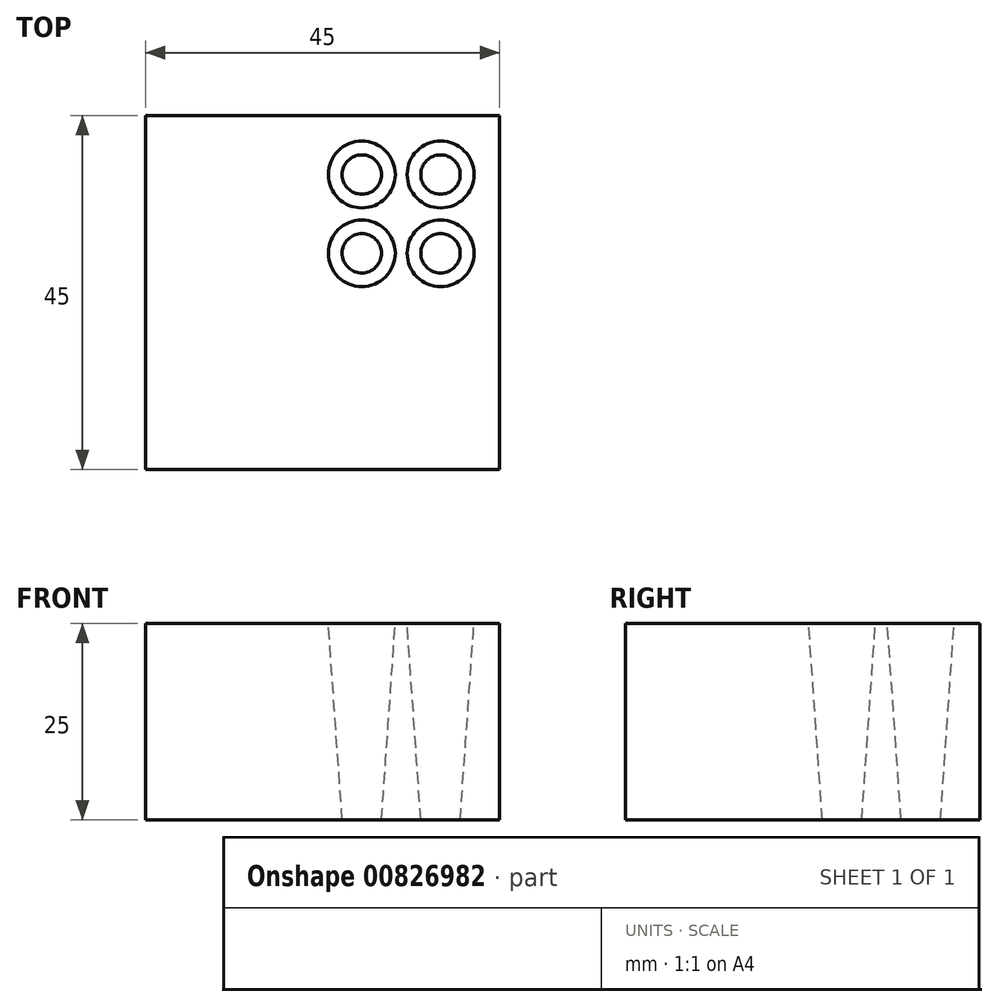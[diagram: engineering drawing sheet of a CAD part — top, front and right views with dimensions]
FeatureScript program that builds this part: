
annotation { "Feature Type Name" : "Feature", "Feature Type Description" : "" }
export const myFeature = defineFeature(function(context is Context, id is Id, definition is map)
    precondition{}
    {
        {
            var Q0;
            Q0=qCreatedBy(makeId("Top.planeOp"),FACE);
            var sketch = newSketch(context, id + "F0", { "sketchPlane" : qUnion([Q0])});
            skLineSegment(sketch, "E0.bottom", {"start": v(-22.5, 22.5) * mm, "end": v(22.5, 22.5) * mm});
            skLineSegment(sketch, "E0.top", {"start": v(-22.5, -22.5) * mm, "end": v(22.5, -22.5) * mm});
            skLineSegment(sketch, "E0.left", {"start": v(-22.5, 22.5) * mm, "end": v(-22.5, -22.5) * mm});
            skLineSegment(sketch, "E0.right", {"start": v(22.5, 22.5) * mm, "end": v(22.5, -22.5) * mm});
            skCircle(sketch, "E1", {"center": v(-15, 15) * mm, "radius": 2.5 * mm});
            skCircle(sketch, "E2", {"center": v(-15, 5) * mm, "radius": 2.5 * mm});
            skCircle(sketch, "E3", {"center": v(-5, 15) * mm, "radius": 2.5 * mm});
            skCircle(sketch, "E4", {"center": v(-5, 5) * mm, "radius": 2.5 * mm});
            skCircle(sketch, "E5.MirrorC", {"center": v(5, 15) * mm, "radius": 2.5 * mm});
            skCircle(sketch, "E6.MirrorC", {"center": v(5, 5) * mm, "radius": 2.5 * mm});
            skCircle(sketch, "E7.MirrorC", {"center": v(15, 5) * mm, "radius": 2.5 * mm});
            skCircle(sketch, "E8.MirrorC", {"center": v(15, 15) * mm, "radius": 2.5 * mm});
            skLineSegment(sketch, "E9.bottom", {"start": v(-12.5, -17.5) * mm, "end": v(-17.5, -17.5) * mm});
            skLineSegment(sketch, "E9.top", {"start": v(-12.5, -12.5) * mm, "end": v(-17.5, -12.5) * mm});
            skLineSegment(sketch, "E9.left", {"start": v(-12.5, -17.5) * mm, "end": v(-12.5, -12.5) * mm});
            skLineSegment(sketch, "E9.right", {"start": v(-17.5, -17.5) * mm, "end": v(-17.5, -12.5) * mm});
            skLineSegment(sketch, "E10.bottom", {"start": v(-2.5, -17.5) * mm, "end": v(-7.5, -17.5) * mm});
            skLineSegment(sketch, "E10.top", {"start": v(-2.5, -12.5) * mm, "end": v(-7.5, -12.5) * mm});
            skLineSegment(sketch, "E10.left", {"start": v(-2.5, -17.5) * mm, "end": v(-2.5, -12.5) * mm});
            skLineSegment(sketch, "E10.right", {"start": v(-7.5, -17.5) * mm, "end": v(-7.5, -12.5) * mm});
            skLineSegment(sketch, "E11.bottom", {"start": v(-2.5, -7.5) * mm, "end": v(-7.5, -7.5) * mm});
            skLineSegment(sketch, "E11.top", {"start": v(-2.5, -2.5) * mm, "end": v(-7.5, -2.5) * mm});
            skLineSegment(sketch, "E11.left", {"start": v(-2.5, -7.5) * mm, "end": v(-2.5, -2.5) * mm});
            skLineSegment(sketch, "E11.right", {"start": v(-7.5, -7.5) * mm, "end": v(-7.5, -2.5) * mm});
            skLineSegment(sketch, "E12.bottom", {"start": v(-12.5, -7.5) * mm, "end": v(-17.5, -7.5) * mm});
            skLineSegment(sketch, "E12.top", {"start": v(-12.5, -2.5) * mm, "end": v(-17.5, -2.5) * mm});
            skLineSegment(sketch, "E12.left", {"start": v(-12.5, -7.5) * mm, "end": v(-12.5, -2.5) * mm});
            skLineSegment(sketch, "E12.right", {"start": v(-17.5, -7.5) * mm, "end": v(-17.5, -2.5) * mm});
            skCircle(sketch, "E13.cCircle", {"center": v(16.06, -15) * mm, "radius": 1.44 * mm, "construction": true});
            skLineSegment(sketch, "E13.0", {"start": v(17.5, -12.5) * mm, "end": v(17.5, -17.5) * mm});
            skLineSegment(sketch, "E13.1", {"start": v(17.5, -17.5) * mm, "end": v(13.17, -15) * mm});
            skLineSegment(sketch, "E13.2", {"start": v(13.17, -15) * mm, "end": v(17.5, -12.5) * mm});
            skPoint(sketch, "E13.0.midPoint", {"position": v(17.5, -15) * mm});
            skLineSegment(sketch, "E14.1.0.0", {"start": v(3.17, -15) * mm, "end": v(7.5, -12.5) * mm});
            skLineSegment(sketch, "E14.1.0.1", {"start": v(7.5, -17.5) * mm, "end": v(3.17, -15) * mm});
            skLineSegment(sketch, "E14.1.0.2", {"start": v(7.5, -12.5) * mm, "end": v(7.5, -17.5) * mm});
            skLineSegment(sketch, "E14.direction1", {"start": v(17.5, -12.5) * mm, "end": v(7.5, -12.5) * mm, "construction": true});
            skLineSegment(sketch, "E15.1.0.0", {"start": v(7.5, -2.5) * mm, "end": v(7.5, -7.5) * mm});
            skLineSegment(sketch, "E15.1.0.1", {"start": v(3.17, -5) * mm, "end": v(7.5, -2.5) * mm});
            skLineSegment(sketch, "E15.1.0.2", {"start": v(7.5, -7.5) * mm, "end": v(3.17, -5) * mm});
            skLineSegment(sketch, "E15.1.0.3", {"start": v(13.17, -5) * mm, "end": v(17.5, -2.5) * mm});
            skLineSegment(sketch, "E15.1.0.4", {"start": v(17.5, -7.5) * mm, "end": v(13.17, -5) * mm});
            skLineSegment(sketch, "E15.1.0.5", {"start": v(17.5, -2.5) * mm, "end": v(17.5, -7.5) * mm});
            skLineSegment(sketch, "E15.1.0.6", {"start": v(22.5, 32.5) * mm, "end": v(22.5, -12.5) * mm});
            skLineSegment(sketch, "E15.direction1", {"start": v(22.5, -22.5) * mm, "end": v(22.5, -12.5) * mm, "construction": true});
            skSolve(sketch);
        }
        {
            var Q0;
            Q0 = qSketchRegion(id + "F0", true);
            extrude(context, id + "F1", {"entities" : qUnion([Q0]), "depth" : 2 * mm, "offsetDistance" : 25 * mm});
        }
        {
            var Q0;
            Q0=makeQuery(id+"F0.imprint","IMPRINT",FACE,{"disambiguationData":[TD([[makeQuery(id+"F0.imprint","IMPRINT",EDGE,{"derivedFrom":sQuery(id+"F0.wireOp",EDGE,"E1")}),1.0]])]});
            var Q1;
            Q1=makeQuery(id+"F0.imprint","IMPRINT",FACE,{"disambiguationData":[TD([[makeQuery(id+"F0.imprint","IMPRINT",EDGE,{"derivedFrom":sQuery(id+"F0.wireOp",EDGE,"E3")}),1.0]])]});
            var Q2;
            Q2=makeQuery(id+"F0.imprint","IMPRINT",FACE,{"disambiguationData":[TD([[makeQuery(id+"F0.imprint","IMPRINT",EDGE,{"derivedFrom":sQuery(id+"F0.wireOp",EDGE,"E5.MirrorC")}),-1.0]])]});
            var Q3;
            Q3=makeQuery(id+"F0.imprint","IMPRINT",FACE,{"disambiguationData":[TD([[makeQuery(id+"F0.imprint","IMPRINT",EDGE,{"derivedFrom":sQuery(id+"F0.wireOp",EDGE,"E8.MirrorC")}),-1.0]])]});
            var Q4;
            Q4=makeQuery(id+"F0.imprint","IMPRINT",FACE,{"disambiguationData":[TD([[makeQuery(id+"F0.imprint","IMPRINT",EDGE,{"derivedFrom":sQuery(id+"F0.wireOp",EDGE,"E7.MirrorC")}),-1.0]])]});
            var Q5;
            Q5=makeQuery(id+"F0.imprint","IMPRINT",FACE,{"disambiguationData":[TD([[makeQuery(id+"F0.imprint","IMPRINT",EDGE,{"derivedFrom":sQuery(id+"F0.wireOp",EDGE,"E6.MirrorC")}),-1.0]])]});
            var Q6;
            Q6=makeQuery(id+"F0.imprint","IMPRINT",FACE,{"disambiguationData":[TD([[makeQuery(id+"F0.imprint","IMPRINT",EDGE,{"derivedFrom":sQuery(id+"F0.wireOp",EDGE,"E4")}),1.0]])]});
            var Q7;
            Q7=makeQuery(id+"F0.imprint","IMPRINT",FACE,{"disambiguationData":[TD([[makeQuery(id+"F0.imprint","IMPRINT",EDGE,{"derivedFrom":sQuery(id+"F0.wireOp",EDGE,"E2")}),1.0]])]});
            var Q8;
            Q8=makeQuery(id+"F0.imprint","IMPRINT",FACE,{"disambiguationData":[TD([[makeQuery(id+"F0.imprint","IMPRINT",EDGE,{"derivedFrom":sQuery(id+"F0.wireOp",EDGE,"8b30ffb8-5058-4532-8c98-71697ab046c90.MirrorC")}),-1.0]])]});
            var Q9;
            Q9=makeQuery(id+"F0.imprint","IMPRINT",FACE,{"disambiguationData":[TD([[makeQuery(id+"F0.imprint","IMPRINT",EDGE,{"derivedFrom":sQuery(id+"F0.wireOp",EDGE,"44b5a80e-55dd-4e2d-ae01-1969e6cece660.MirrorC")}),-1.0]])]});
            var Q10;
            Q10=makeQuery(id+"F0.imprint","IMPRINT",FACE,{"disambiguationData":[TD([[makeQuery(id+"F0.imprint","IMPRINT",EDGE,{"derivedFrom":sQuery(id+"F0.wireOp",EDGE,"2a1f1990-0ffb-4feb-9302-70185462b3990.MirrorC")}),1.0]])]});
            var Q11;
            Q11=makeQuery(id+"F0.imprint","IMPRINT",FACE,{"disambiguationData":[TD([[makeQuery(id+"F0.imprint","IMPRINT",EDGE,{"derivedFrom":sQuery(id+"F0.wireOp",EDGE,"1551ad50-0c97-479f-8c74-bc045f3996530.MirrorC")}),1.0]])]});
            var Q12;
            Q12=makeQuery(id+"F0.imprint","IMPRINT",FACE,{"disambiguationData":[TD([[makeQuery(id+"F0.imprint","IMPRINT",EDGE,{"derivedFrom":sQuery(id+"F0.wireOp",EDGE,"9e5614db-67e3-4650-9598-719f54ae0f6b0.MirrorC")}),1.0]])]});
            var Q13;
            Q13=makeQuery(id+"F0.imprint","IMPRINT",FACE,{"disambiguationData":[TD([[makeQuery(id+"F0.imprint","IMPRINT",EDGE,{"derivedFrom":sQuery(id+"F0.wireOp",EDGE,"e295cbc7-ad30-4c96-aff9-b1009714e4b60.MirrorC")}),1.0]])]});
            var Q14;
            Q14=makeQuery(id+"F0.imprint","IMPRINT",FACE,{"disambiguationData":[TD([[makeQuery(id+"F0.imprint","IMPRINT",EDGE,{"derivedFrom":sQuery(id+"F0.wireOp",EDGE,"23d3eaa0-47f1-4570-9f4c-0a46f516fc930.MirrorC")}),-1.0]])]});
            var Q15;
            Q15=makeQuery(id+"F0.imprint","IMPRINT",FACE,{"disambiguationData":[TD([[makeQuery(id+"F0.imprint","IMPRINT",EDGE,{"derivedFrom":sQuery(id+"F0.wireOp",EDGE,"b4c0c9e2-75f3-4258-bb03-8fbac0f7afba0.MirrorC")}),-1.0]])]});
            var Q16;
            Q16=makeQuery(id+"F0.imprint","IMPRINT",FACE,{"disambiguationData":[TD([[makeQuery(id+"F0.imprint","IMPRINT",EDGE,{"derivedFrom":sQuery(id+"F0.wireOp",EDGE,"E11.bottom")}),-1.0]])]});
            var Q17;
            Q17=makeQuery(id+"F0.imprint","IMPRINT",FACE,{"disambiguationData":[TD([[makeQuery(id+"F0.imprint","IMPRINT",EDGE,{"derivedFrom":sQuery(id+"F0.wireOp",EDGE,"E12.bottom")}),-1.0]])]});
            var Q18;
            Q18=makeQuery(id+"F0.imprint","IMPRINT",FACE,{"disambiguationData":[TD([[makeQuery(id+"F0.imprint","IMPRINT",EDGE,{"derivedFrom":sQuery(id+"F0.wireOp",EDGE,"E9.bottom")}),-1.0]])]});
            var Q19;
            Q19=makeQuery(id+"F0.imprint","IMPRINT",FACE,{"disambiguationData":[TD([[makeQuery(id+"F0.imprint","IMPRINT",EDGE,{"derivedFrom":sQuery(id+"F0.wireOp",EDGE,"E10.bottom")}),-1.0]])]});
            var Q20;
            Q20=makeQuery(id+"F0.imprint","IMPRINT",FACE,{"disambiguationData":[TD([[makeQuery(id+"F0.imprint","IMPRINT",EDGE,{"derivedFrom":sQuery(id+"F0.wireOp",EDGE,"E15.1.0.0")}),-1.0]])]});
            var Q21;
            Q21=makeQuery(id+"F0.imprint","IMPRINT",FACE,{"disambiguationData":[TD([[makeQuery(id+"F0.imprint","IMPRINT",EDGE,{"derivedFrom":sQuery(id+"F0.wireOp",EDGE,"E15.1.0.3")}),-1.0]])]});
            var Q22;
            Q22=makeQuery(id+"F0.imprint","IMPRINT",FACE,{"disambiguationData":[TD([[makeQuery(id+"F0.imprint","IMPRINT",EDGE,{"derivedFrom":sQuery(id+"F0.wireOp",EDGE,"E14.1.0.0")}),-1.0]])]});
            var Q23;
            Q23=makeQuery(id+"F0.imprint","IMPRINT",FACE,{"disambiguationData":[TD([[makeQuery(id+"F0.imprint","IMPRINT",EDGE,{"derivedFrom":sQuery(id+"F0.wireOp",EDGE,"E13.0")}),-1.0]])]});
            extrude(context, id + "F2", {"entities" : qUnion([Q0, Q1, Q2, Q3, Q4, Q5, Q6, Q7, Q8, Q9, Q10, Q11, Q12, Q13, Q14, Q15, Q16, Q17, Q18, Q19, Q20, Q21, Q22, Q23]), "operationType" : NewBodyOperationType.ADD, "depth" : 25 * mm, "offsetDistance" : 25 * mm});
        }
        {
            var Q0;
            Q0=makeQuery(id+"F2.opExtrude","CAP_EDGE",EDGE,{"disambiguationData":[OSD([sQuery(id+"F0.wireOp",EDGE,"E8.MirrorC")])],"isStart":false});
            var Q1;
            Q1=makeQuery(id+"F2.opExtrude","CAP_EDGE",EDGE,{"disambiguationData":[OSD([sQuery(id+"F0.wireOp",EDGE,"E7.MirrorC")])],"isStart":false});
            var Q2;
            Q2=makeQuery(id+"F2.opExtrude","CAP_EDGE",EDGE,{"disambiguationData":[OSD([sQuery(id+"F0.wireOp",EDGE,"E6.MirrorC")])],"isStart":false});
            var Q3;
            Q3=makeQuery(id+"F2.opExtrude","CAP_EDGE",EDGE,{"disambiguationData":[OSD([sQuery(id+"F0.wireOp",EDGE,"E5.MirrorC")])],"isStart":false});
            chamfer(context, id + "F3", {"entities" : qUnion([Q0, Q1, Q2, Q3]), "chamferType" : ChamferType.OFFSET_ANGLE, "width" : 25 * mm, "oppositeDirection" : false, "angle" : 4 * degree, "tangentPropagation" : true});
        }
    });
